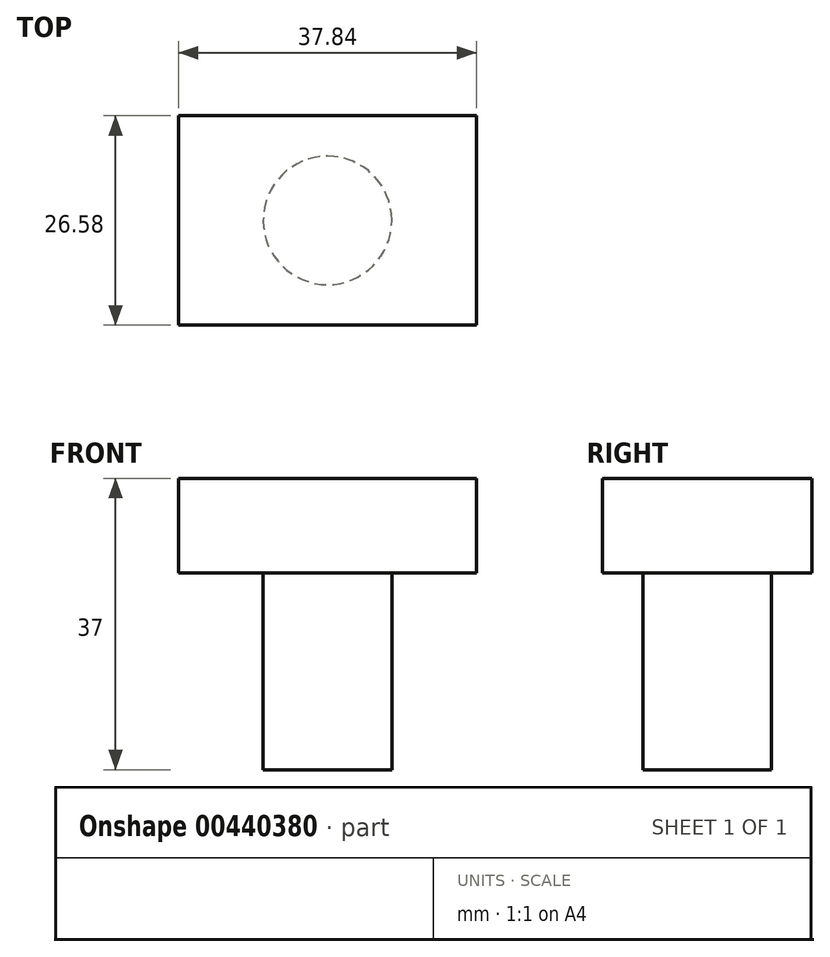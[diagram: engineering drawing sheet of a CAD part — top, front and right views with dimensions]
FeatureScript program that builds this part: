
annotation { "Feature Type Name" : "Feature", "Feature Type Description" : "" }
export const myFeature = defineFeature(function(context is Context, id is Id, definition is map)
    precondition{}
    {
        {
            var Q0;
            Q0=qCreatedBy(makeId("Top.planeOp"),FACE);
            var sketch = newSketch(context, id + "F0", { "sketchPlane" : qUnion([Q0])});
            skLineSegment(sketch, "E0.bottom", {"start": v(-18.92, -13.3) * mm, "end": v(18.92, -13.3) * mm});
            skLineSegment(sketch, "E0.top", {"start": v(-18.92, 13.3) * mm, "end": v(18.92, 13.3) * mm});
            skLineSegment(sketch, "E0.left", {"start": v(-18.92, -13.3) * mm, "end": v(-18.92, 13.3) * mm});
            skLineSegment(sketch, "E0.right", {"start": v(18.92, -13.3) * mm, "end": v(18.92, 13.3) * mm});
            skPoint(sketch, "E0.middle", {"position": v(0, 0) * mm});
            skSolve(sketch);
        }
        {
            var Q0;
            Q0=makeQuery(id+"F0.imprint","IMPRINT",FACE,{"disambiguationData":[TD([[makeQuery(id+"F0.imprint","IMPRINT",EDGE,{"derivedFrom":sQuery(id+"F0.wireOp",EDGE,"E0.bottom")}),1.0]])]});
            extrude(context, id + "F1", {"entities" : qUnion([Q0]), "oppositeDirection" : true, "depth" : 12 * mm});
        }
        {
            var Q0;
            Q0=makeQuery(id+"F1.opExtrude","CAP_FACE",FACE,{"disambiguationData":[OSD([sQuery(id+"F0.wireOp",EDGE,"E0.bottom"),sQuery(id+"F0.wireOp",EDGE,"E0.top"),sQuery(id+"F0.wireOp",EDGE,"E0.left"),sQuery(id+"F0.wireOp",EDGE,"E0.right")])],"isStart":false});
            var sketch = newSketch(context, id + "F2", { "sketchPlane" : qUnion([Q0])});
            skCircle(sketch, "E1", {"center": v(0, 0) * mm, "radius": 8.16 * mm});
            skSolve(sketch);
        }
        {
            var Q0;
            Q0=makeQuery(id+"F2.imprint","IMPRINT",FACE,{"disambiguationData":[TD([[makeQuery(id+"F2.imprint","IMPRINT",EDGE,{"derivedFrom":sQuery(id+"F2.wireOp",EDGE,"E1")}),1.0]])]});
            extrude(context, id + "F3", {"entities" : qUnion([Q0]), "operationType" : NewBodyOperationType.ADD, "depth" : 25 * mm});
        }
    });
